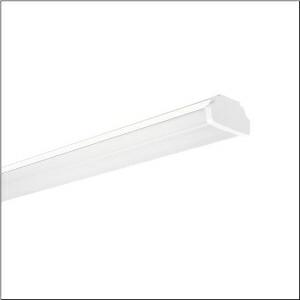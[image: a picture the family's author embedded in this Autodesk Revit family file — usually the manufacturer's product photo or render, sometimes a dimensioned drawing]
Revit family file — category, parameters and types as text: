
# Revit family: modario_r__31_ho_53bm812m1v4120_c9f3
name_source: partatom
category: Lighting Fixtures
units: mm (PartAtom-declared; Revit-internal decimal feet)

## family parameters
Cut with Voids When Loaded = No
Host = Face
Light Source = No
Part Type = Normal
Room Calculation Point = No
Round Connector Dimension = Use Diameter
Shared = No

## types (1)
- --- (1 x LED, 12380 lm, 77.3 W, 4000K)
    Apparent Load = 77 VA
    CIE Flux Codes = 47 80 95 92 100
    Color Rendering = 80
    Color Temperature = 4000K
    Default Elevation = 1800 mm
    Description = Modario® 31 HO, luminaire insert, of sheet steel, coil coated, white, length: 1.495mm, width: 81mm, height: 82mm, 5x system unit, system units: 299mm, LED rated luminous flux: 12.380lm, light colour: 840, control gear: ON/OFF Multilumen, control gear: ECG Multilumen, with plug, 3-pole, with phase selection, mains connection: 220..240V, AC, 50/60Hz, rated input power: 77W, through-wiring accessed according to module size, primary optical cover: cover, of PMMA, light emission: direct distribution, primary light characteristic: symmetric, protection rating (complete): IP20, protection rating (LED compartment): IP50, insulation class (complete): insulation class I (protective earthing), certification: CE, ENEC, VDE, UKCA, impact resistance: IK03, permissible ambient temperature for indoor applications: -35..+35°C, corresponds to IFS (International Featured Standards) requirements for safety and quality in the food industry, reducing of maximum allowable ambient temperature of 5°C with ceiling mounting, packaging unit: 1 piece
    Height = 92 mm
    Lamp = 1 x LED
    Lamp Light Flux = 12380 lm
    Lamp Power = 77.3 W
    Lamp count = 1
    Length = 1495 mm
    Luminous efficacy = 160 lm/W
    Manufacturer = Siteco
    ModVariant = No
    Model = 53BM812M1V4120
    Mounting Place = Ceiling
    Mounting Type = Pendant
    Number of Poles = 1
    OnlyDefault = Yes
    Power Factor = 1
    Product Name = Modario® 31 HO
    Product group = luminaire insert | ceiling pendant
    ProductGroupID = 902
    Protection Class = Protection class I
    Protection Degree = IP 20
    RLX_Detail_Level = 1
    RLX_Emergency_Light_Flux = 0 lm
    RLX_Emergency_Type = 0
    RLX_Emergency_Type_DB = No
    RlxData = <blob elided: 40141 chars, md5=597b73e8>
    Socket = socket
    Standby Power = 0 W
    System Light Flux = 12380 lm
    System Power = 77 W
    Type Comments = factory setting: luminous flux: 100 % | (A | C | E) | 173 mA
    Type Image = l_1341886.jpg
    URL = http://relux.com
    VarID = @adj_219645
    Voltage = 0 V
    Weight = 0.00 kg
    Width = 81 mm

## geometry (parser evidence)
native form markers: Blend x4, Sweep x10
no freeform markers — native parametric forms only
